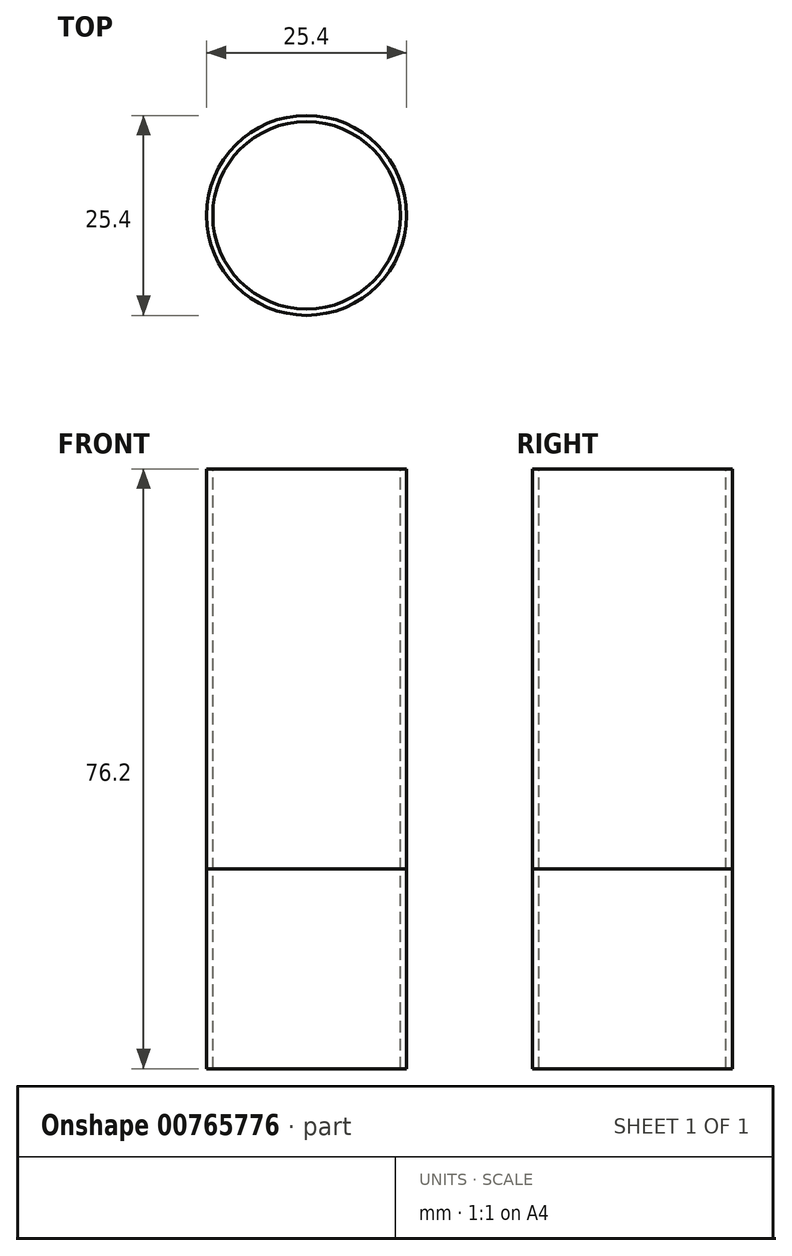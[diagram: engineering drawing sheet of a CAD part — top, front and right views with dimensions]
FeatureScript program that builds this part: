
annotation { "Feature Type Name" : "Feature", "Feature Type Description" : "" }
export const myFeature = defineFeature(function(context is Context, id is Id, definition is map)
    precondition{}
    {
        {
            var Q0;
            Q0=qCreatedBy(makeId("Top.planeOp"),FACE);
            var sketch = newSketch(context, id + "F0", { "sketchPlane" : qUnion([Q0])});
            skCircle(sketch, "E0", {"center": v(0, 0) * mm, "radius": 12.7 * mm});
            skCircle(sketch, "E1", {"center": v(0, 0) * mm, "radius": 11.9 * mm});
            skSolve(sketch);
        }
        {
            var Q0;
            Q0=sQuery(id+"F0.wireOp",EDGE,"E1");
            var Q1;
            Q1=sQuery(id+"F0.wireOp",EDGE,"E0");
            extrude(context, id + "F1", {"bodyType" : ToolBodyType.SURFACE, "surfaceEntities" : qUnion([Q0, Q1]), "depth" : 76.2 * mm, "offsetDistance" : 25.4 * mm});
        }
        {
            var Q0;
            Q0=qCreatedBy(makeId("Top.planeOp"),FACE);
            var sketch = newSketch(context, id + "F2", { "sketchPlane" : qUnion([Q0])});
            skCircle(sketch, "E2", {"center": v(0, 0) * mm, "radius": 12.7 * mm});
            skSolve(sketch);
        }
        {
            var Q0;
            Q0=sQuery(id+"F2.wireOp",EDGE,"E2");
            extrude(context, id + "F3", {"bodyType" : ToolBodyType.SURFACE, "surfaceEntities" : qUnion([Q0]), "depth" : 25.4 * mm, "offsetDistance" : 25.4 * mm});
        }
    });
